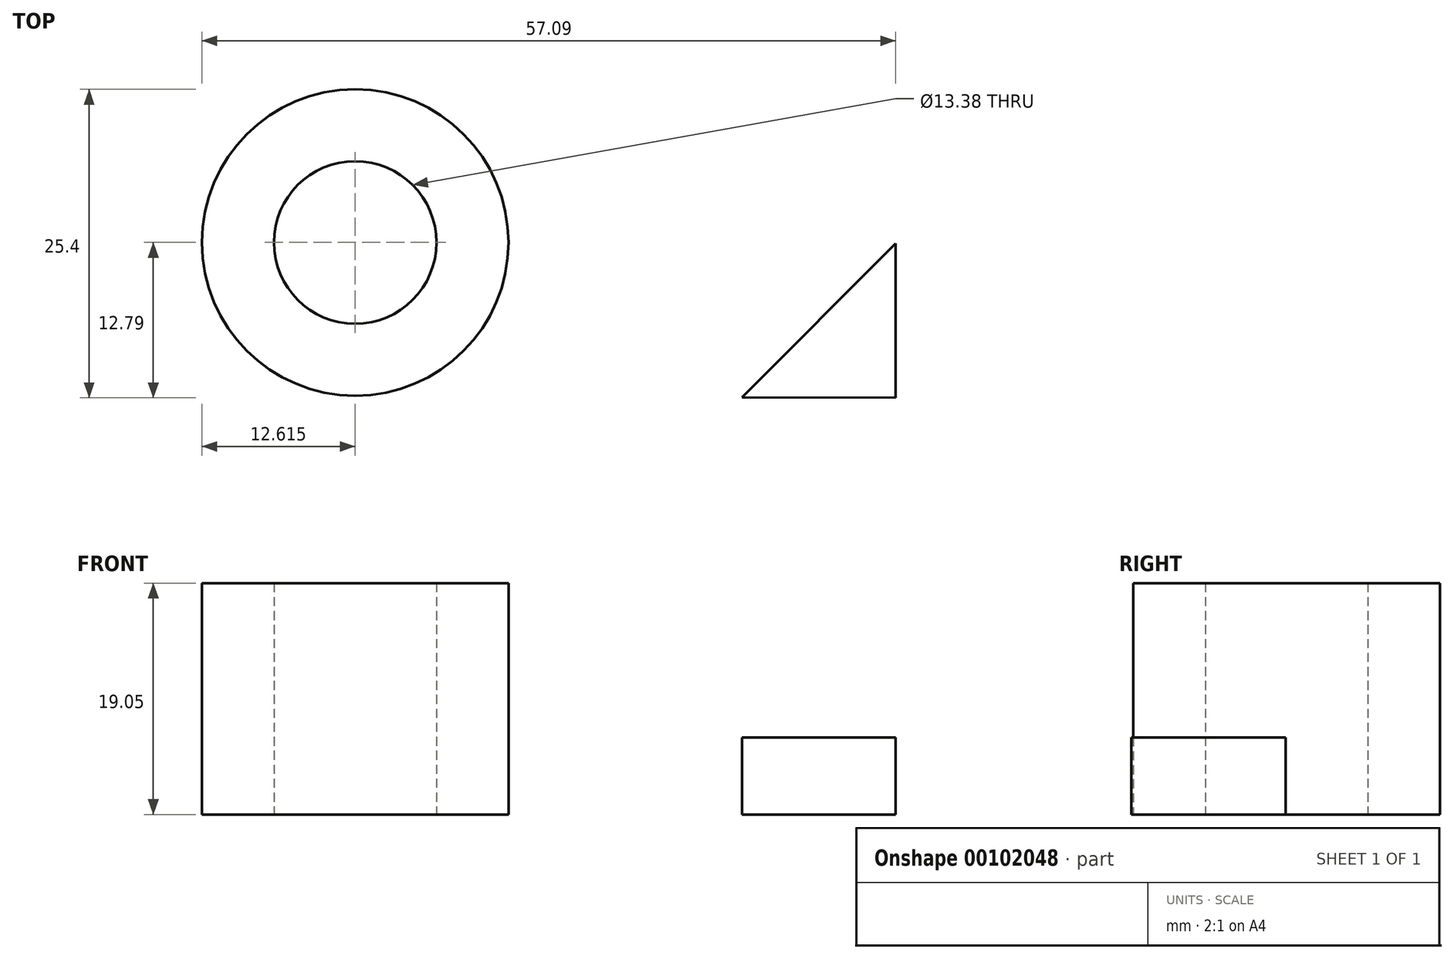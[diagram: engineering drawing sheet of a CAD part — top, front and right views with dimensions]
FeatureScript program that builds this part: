
annotation { "Feature Type Name" : "Feature", "Feature Type Description" : "" }
export const myFeature = defineFeature(function(context is Context, id is Id, definition is map)
    precondition{}
    {
        {
            var Q0;
            Q0=qCreatedBy(makeId("Top.planeOp"),FACE);
            var sketch = newSketch(context, id + "F0", { "sketchPlane" : qUnion([Q0])});
            skLineSegment(sketch, "E0", {"start": v(57.15, -0.09) * mm, "end": v(57.15, 25.31) * mm});
            skCircle(sketch, "E1", {"center": v(12.68, 12.7) * mm, "radius": 12.61 * mm});
            skCircle(sketch, "E2", {"center": v(12.68, 12.7) * mm, "radius": 6.69 * mm});
            skLineSegment(sketch, "E3", {"start": v(57.15, -0.09) * mm, "end": v(57.15, 12.61) * mm});
            skLineSegment(sketch, "E4", {"start": v(57.15, -0.09) * mm, "end": v(44.45, -0.09) * mm});
            skLineSegment(sketch, "E5", {"start": v(44.45, -0.09) * mm, "end": v(57.15, 12.61) * mm});
            skLineSegment(sketch, "E6", {"start": v(57.15, 25.31) * mm, "end": v(12.68, 25.31) * mm});
            skLineSegment(sketch, "E7", {"start": v(57.15, -0.09) * mm, "end": v(12.68, 0.09) * mm});
            skSolve(sketch);
        }
        {
            var Q0;
            Q0=makeQuery(id+"F0.imprint","IMPRINT",FACE,{"disambiguationData":[TD([[makeQuery(id+"F0.imprint","IMPRINT",EDGE,{"derivedFrom":sQuery(id+"F0.wireOp",EDGE,"E2")}),-1.0]])]});
            extrude(context, id + "F1", {"entities" : qUnion([Q0]), "depth" : 19.05 * mm});
        }
        {
            var Q0;
            {var subQ2=sQuery(id+"F0.wireOp",EDGE,"E0");Q0=makeQuery(id+"F0.imprint","IMPRINT",FACE,{"disambiguationData":[TD([[makeQuery(id+"F0.imprint","IMPRINT",EDGE,{"derivedFrom":subQ2}),1.0]])]});}
            extrude(context, id + "F2", {"entities" : qUnion([Q0]), "operationType" : NewBodyOperationType.ADD, "depth" : 6.35 * mm});
        }
    });
